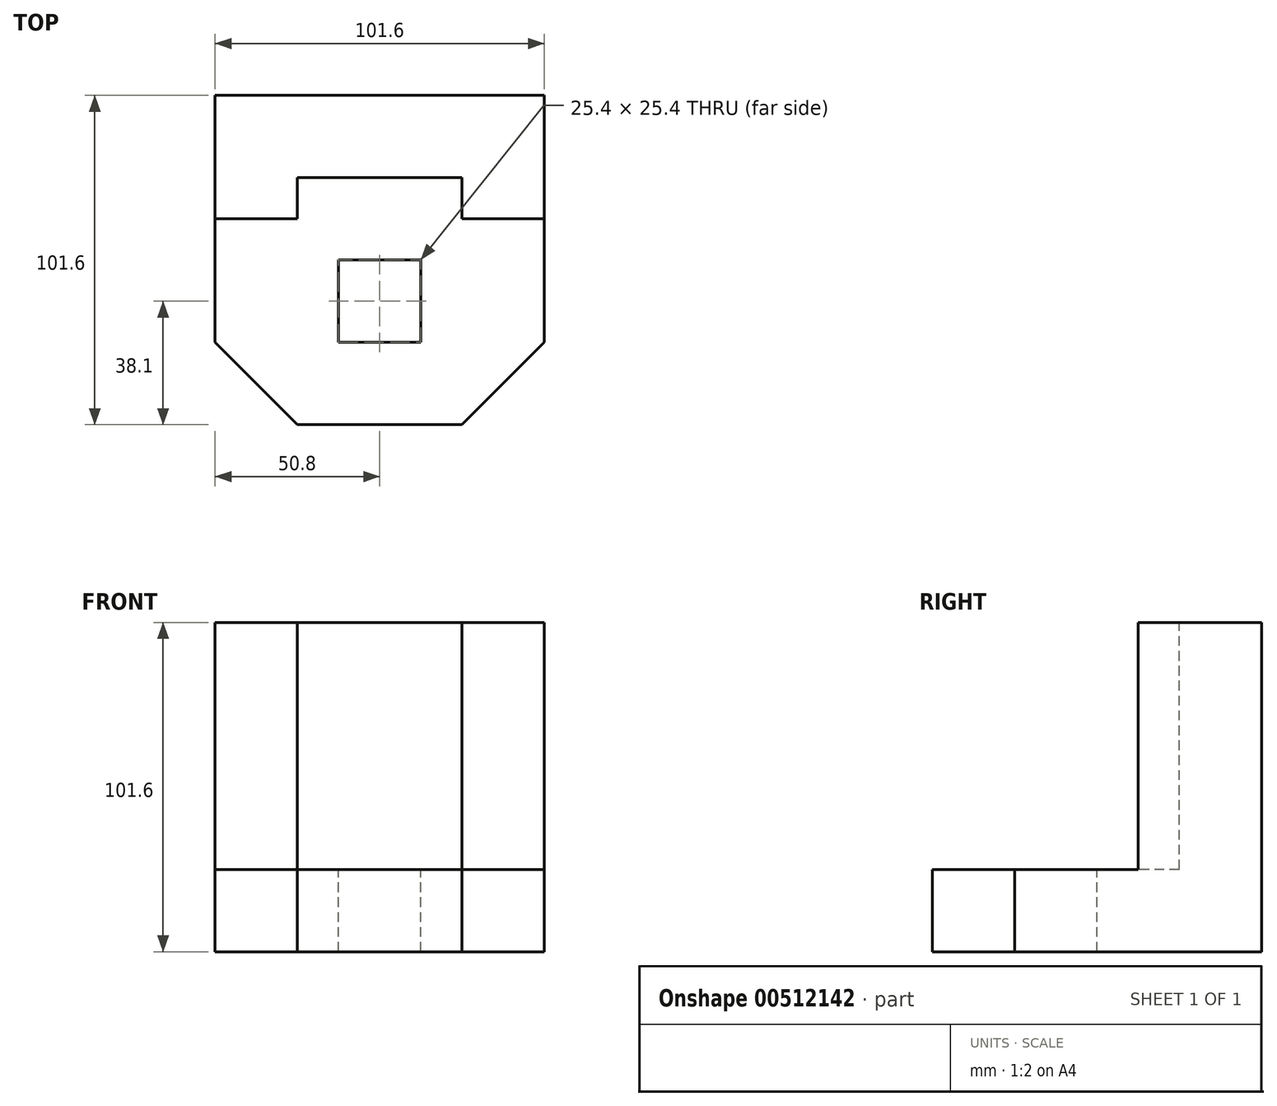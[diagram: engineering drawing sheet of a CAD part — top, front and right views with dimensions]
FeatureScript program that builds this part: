
annotation { "Feature Type Name" : "Feature", "Feature Type Description" : "" }
export const myFeature = defineFeature(function(context is Context, id is Id, definition is map)
    precondition{}
    {
        {
            var Q0;
            Q0=qCreatedBy(makeId("Front.planeOp"),FACE);
            var sketch = newSketch(context, id + "F0", { "sketchPlane" : qUnion([Q0])});
            skLineSegment(sketch, "E0.bottom", {"start": v(0, 0) * mm, "end": v(-101.6, 0) * mm});
            skLineSegment(sketch, "E0.top", {"start": v(0, 101.6) * mm, "end": v(-101.6, 101.6) * mm});
            skLineSegment(sketch, "E0.left", {"start": v(0, 0) * mm, "end": v(0, 101.6) * mm});
            skLineSegment(sketch, "E0.right", {"start": v(-101.6, 0) * mm, "end": v(-101.6, 101.6) * mm});
            skSolve(sketch);
        }
        {
            var Q0;
            Q0=makeQuery(id+"F0.imprint","IMPRINT",FACE,{"disambiguationData":[TD([[makeQuery(id+"F0.imprint","IMPRINT",EDGE,{"derivedFrom":sQuery(id+"F0.wireOp",EDGE,"E0.bottom")}),-1.0]])]});
            extrude(context, id + "F1", {"entities" : qUnion([Q0]), "depth" : 101.6 * mm});
        }
        {
            var Q0;
            Q0=makeQuery(id+"F1.opExtrude","SWEPT_FACE",FACE,{"disambiguationData":[OSD([sQuery(id+"F0.wireOp",EDGE,"E0.left")])]});
            var sketch = newSketch(context, id + "F2", { "sketchPlane" : qUnion([Q0])});
            skLineSegment(sketch, "E1", {"start": v(-101.6, 0) * mm, "end": v(-101.6, 25.4) * mm});
            skLineSegment(sketch, "E2", {"start": v(-101.6, 25.4) * mm, "end": v(-38.1, 25.4) * mm});
            skLineSegment(sketch, "E3", {"start": v(-38.1, 25.4) * mm, "end": v(-38.1, 101.6) * mm});
            skLineSegment(sketch, "E4", {"start": v(-38.1, 101.6) * mm, "end": v(-38.1, 25.4) * mm});
            skSolve(sketch);
        }
        {
            var Q0;
            {var subQ0=sQuery(id+"F2.wireOp",EDGE,"E2");Q0=makeQuery(id+"F2.imprint","IMPRINT",FACE,{"disambiguationData":[TD([[makeQuery(id+"F2.imprint","IMPRINT",EDGE,{"derivedFrom":subQ0}),1.0]])]});}
            extrude(context, id + "F3", {"entities" : qUnion([Q0]), "operationType" : NewBodyOperationType.REMOVE, "oppositeDirection" : true, "depth" : 127 * mm});
        }
        {
            var Q0;
            Q0=makeQuery(id+"F3.boolean.opBoolean","COPY",FACE,{"derivedFrom":makeQuery(id+"F3.opExtrude","SWEPT_FACE",FACE,{"disambiguationData":[OSD([sQuery(id+"F2.wireOp",EDGE,"E2")])]})});
            var sketch = newSketch(context, id + "F4", { "sketchPlane" : qUnion([Q0])});
            skLineSegment(sketch, "E5", {"start": v(0, -101.6) * mm, "end": v(0, -76.2) * mm});
            skLineSegment(sketch, "E6", {"start": v(0, -76.2) * mm, "end": v(-25.4, -76.2) * mm});
            skLineSegment(sketch, "E7", {"start": v(-25.4, -76.2) * mm, "end": v(-25.4, -101.6) * mm});
            skLineSegment(sketch, "E8", {"start": v(-25.4, -101.6) * mm, "end": v(0, -76.2) * mm});
            skSolve(sketch);
        }
        {
            var Q0;
            {var subQ0=sQuery(id+"F4.wireOp",EDGE,"E5");Q0=makeQuery(id+"F4.imprint","IMPRINT",FACE,{"disambiguationData":[TD([[makeQuery(id+"F4.imprint","IMPRINT",EDGE,{"derivedFrom":subQ0}),1.0]])]});}
            extrude(context, id + "F5", {"entities" : qUnion([Q0]), "operationType" : NewBodyOperationType.REMOVE, "oppositeDirection" : true, "depth" : 25.4 * mm});
        }
        {
            var Q0;
            Q0=makeQuery(id+"F3.boolean.opBoolean","COPY",FACE,{"derivedFrom":makeQuery(id+"F3.opExtrude","SWEPT_FACE",FACE,{"disambiguationData":[OSD([sQuery(id+"F2.wireOp",EDGE,"E2")])]})});
            var sketch = newSketch(context, id + "F6", { "sketchPlane" : qUnion([Q0])});
            skLineSegment(sketch, "E9", {"start": v(-101.6, -101.6) * mm, "end": v(-101.6, -76.2) * mm});
            skLineSegment(sketch, "E10", {"start": v(-101.6, -76.2) * mm, "end": v(-76.2, -76.2) * mm});
            skLineSegment(sketch, "E11", {"start": v(-76.2, -76.2) * mm, "end": v(-76.2, -101.6) * mm});
            skLineSegment(sketch, "E12", {"start": v(-76.2, -101.6) * mm, "end": v(-101.6, -101.6) * mm});
            skLineSegment(sketch, "E13", {"start": v(-101.6, -76.2) * mm, "end": v(-76.2, -101.6) * mm});
            skSolve(sketch);
        }
        {
            var Q0;
            Q0=makeQuery(id+"F6.imprint","IMPRINT",FACE,{"disambiguationData":[TD([[makeQuery(id+"F6.imprint","IMPRINT",EDGE,{"derivedFrom":sQuery(id+"F6.wireOp",EDGE,"E9")}),1.0]])]});
            extrude(context, id + "F7", {"entities" : qUnion([Q0]), "operationType" : NewBodyOperationType.REMOVE, "oppositeDirection" : true, "depth" : 25.4 * mm});
        }
        {
            var Q0;
            Q0=makeQuery(id+"F1.opExtrude","SWEPT_FACE",FACE,{"disambiguationData":[OSD([sQuery(id+"F0.wireOp",EDGE,"E0.top")])]});
            var sketch = newSketch(context, id + "F8", { "sketchPlane" : qUnion([Q0])});
            skLineSegment(sketch, "E14", {"start": v(-101.6, -38.1) * mm, "end": v(-76.2, -38.1) * mm});
            skLineSegment(sketch, "E15", {"start": v(-76.2, -38.1) * mm, "end": v(-76.2, -25.4) * mm});
            skLineSegment(sketch, "E16", {"start": v(-76.2, -25.4) * mm, "end": v(-25.4, -25.4) * mm});
            skLineSegment(sketch, "E17", {"start": v(-25.4, -25.4) * mm, "end": v(-25.4, -38.1) * mm});
            skSolve(sketch);
        }
        {
            var Q0;
            {var subQ0=sQuery(id+"F8.wireOp",EDGE,"E15");Q0=makeQuery(id+"F8.imprint","IMPRINT",FACE,{"disambiguationData":[TD([[makeQuery(id+"F8.imprint","IMPRINT",EDGE,{"derivedFrom":subQ0}),-1.0]])]});}
            extrude(context, id + "F9", {"entities" : qUnion([Q0]), "operationType" : NewBodyOperationType.REMOVE, "oppositeDirection" : true, "depth" : 76.2 * mm});
        }
        {
            var Q0;
            Q0=makeQuery(id+"F9.boolean.opBoolean","MERGE",FACE,{"derivedFrom":[makeQuery(id+"F3.boolean.opBoolean","COPY",FACE,{"derivedFrom":makeQuery(id+"F3.opExtrude","SWEPT_FACE",FACE,{"disambiguationData":[OSD([sQuery(id+"F2.wireOp",EDGE,"E2")])]})}),makeQuery(id+"F9.opExtrude","CAP_FACE",FACE,{"disambiguationData":[OSD([sQuery(id+"F0.wireOp",EDGE,"E0.top"),sQuery(id+"F0.wireOp",EDGE,"E0.left"),sQuery(id+"F2.wireOp",EDGE,"E4"),sQuery(id+"F8.wireOp",EDGE,"E15"),sQuery(id+"F8.wireOp",EDGE,"E16"),sQuery(id+"F8.wireOp",EDGE,"E17")])],"isStart":false})]});
            var sketch = newSketch(context, id + "F10", { "sketchPlane" : qUnion([Q0])});
            skLineSegment(sketch, "E18", {"start": v(0, -76.2) * mm, "end": v(-38.1, -76.2) * mm});
            skLineSegment(sketch, "E19", {"start": v(-38.1, -76.2) * mm, "end": v(-63.5, -76.2) * mm});
            skLineSegment(sketch, "E20", {"start": v(-63.5, -76.2) * mm, "end": v(-63.5, -50.8) * mm});
            skLineSegment(sketch, "E21", {"start": v(-63.5, -50.8) * mm, "end": v(-38.1, -50.8) * mm});
            skLineSegment(sketch, "E22", {"start": v(-38.1, -50.8) * mm, "end": v(-38.1, -76.2) * mm});
            skSolve(sketch);
        }
        {
            var Q0;
            Q0=makeQuery(id+"F10.imprint","IMPRINT",FACE,{"disambiguationData":[TD([[makeQuery(id+"F10.imprint","IMPRINT",EDGE,{"derivedFrom":sQuery(id+"F10.wireOp",EDGE,"E19")}),-1.0]])]});
            extrude(context, id + "F11", {"entities" : qUnion([Q0]), "operationType" : NewBodyOperationType.REMOVE, "oppositeDirection" : true, "depth" : 127 * mm});
        }
    });
